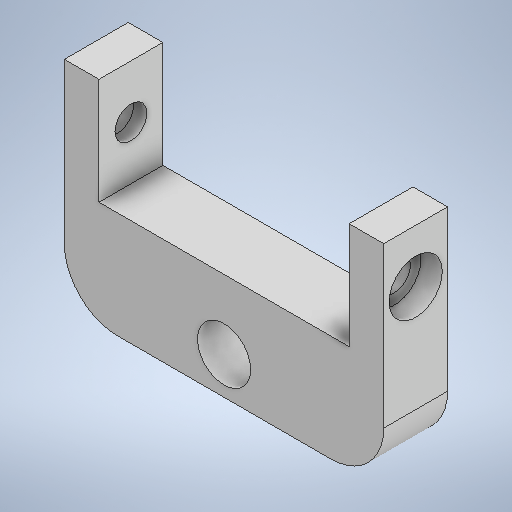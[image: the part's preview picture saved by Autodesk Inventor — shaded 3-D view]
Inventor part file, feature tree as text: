
AUTODESK INVENTOR PART (.ipt)
format: ipt  version: 2025.3 (Build 293356000, 356)  size: 248,320 bytes
history: native  units: mm
features: other x2, sketch x2, extrude x1, hole x1, mirror x1, fillet x1
ambient origin geometry x8: Origin, YZ Plane, XZ Plane, XY Plane, X Axis, Y Axis, Z Axis, Center Point
bodies: Body1 (feature_tree)
feature tree (8):
  other  "솔리드1"
  extrude  "돌출1"  Depth=23.5mm
  hole  "구멍1"  [1 undecoded]
  other  "작업 평면1"
  mirror  "미러1"
  fillet  "모깎기1"  Radius=30.0mm
  sketch  "스케치1"
  sketch  "스케치2"
note: 1 required parameter value undecoded (feature->parameter linkage not recoverable at this tier; creation-order binding heuristic only, values carry confidence <= 0.55)
